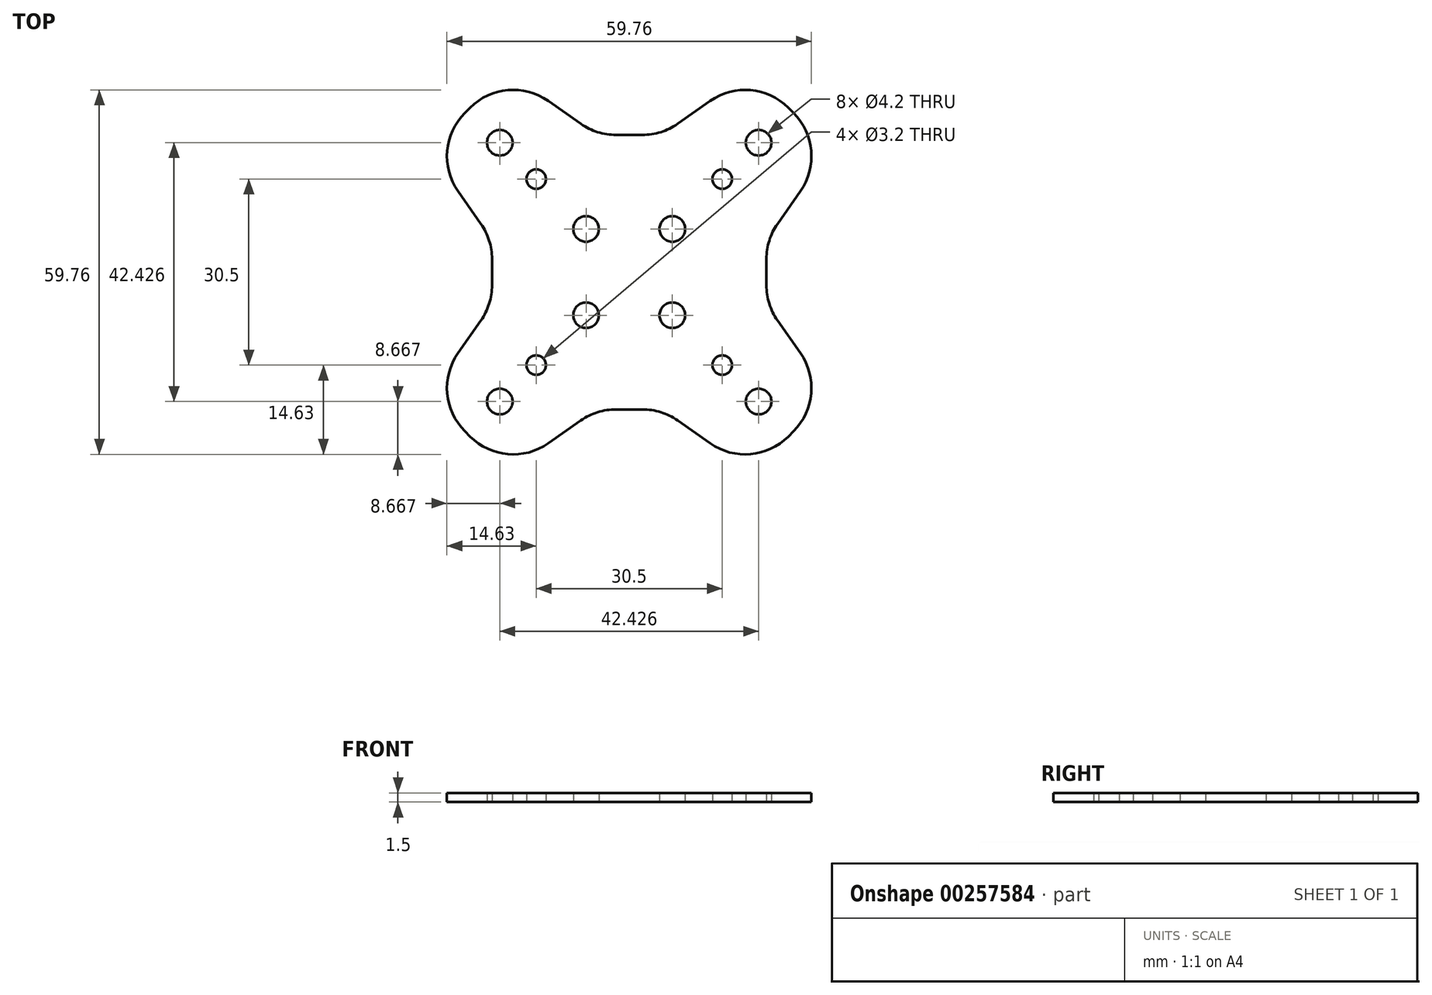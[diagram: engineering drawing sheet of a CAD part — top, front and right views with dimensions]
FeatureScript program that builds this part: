
annotation { "Feature Type Name" : "Feature", "Feature Type Description" : "" }
export const myFeature = defineFeature(function(context is Context, id is Id, definition is map)
    precondition{}
    {
        {
            var Q0;
            Q0=qCreatedBy(makeId("Top.planeOp"),FACE);
            var sketch = newSketch(context, id + "F0", { "sketchPlane" : qUnion([Q0])});
            skLineSegment(sketch, "E0", {"start": v(-32.88, 20.15) * mm, "end": v(-20.15, 32.88) * mm});
            skLineSegment(sketch, "E1", {"start": v(-20.15, 32.88) * mm, "end": v(-5.33, 22.5) * mm});
            skLineSegment(sketch, "E2", {"start": v(-32.88, 20.15) * mm, "end": v(-22.5, 5.33) * mm});
            skLineSegment(sketch, "E3", {"start": v(0, 0) * mm, "end": v(-26.52, 26.52) * mm, "construction": true});
            skLineSegment(sketch, "E4.MirrorCS", {"start": v(32.88, 20.15) * mm, "end": v(20.15, 32.88) * mm});
            skLineSegment(sketch, "E5.MirrorCS", {"start": v(32.88, 20.15) * mm, "end": v(22.5, 5.33) * mm});
            skLineSegment(sketch, "E6.MirrorCS", {"start": v(20.15, 32.88) * mm, "end": v(5.33, 22.5) * mm});
            skLineSegment(sketch, "E7.MirrorCS", {"start": v(20.15, -32.88) * mm, "end": v(5.33, -22.5) * mm});
            skLineSegment(sketch, "E8.MirrorCS", {"start": v(-32.88, -20.15) * mm, "end": v(-20.15, -32.88) * mm});
            skLineSegment(sketch, "E9.MirrorCS", {"start": v(32.88, -20.15) * mm, "end": v(22.5, -5.33) * mm});
            skLineSegment(sketch, "E10.MirrorCS", {"start": v(-32.88, -20.15) * mm, "end": v(-22.5, -5.33) * mm});
            skLineSegment(sketch, "E11.MirrorCS", {"start": v(-20.15, -32.88) * mm, "end": v(-5.33, -22.5) * mm});
            skLineSegment(sketch, "E12.MirrorCS", {"start": v(32.88, -20.15) * mm, "end": v(20.15, -32.88) * mm});
            skLineSegment(sketch, "E13", {"start": v(-5.33, 22.5) * mm, "end": v(5.33, 22.5) * mm});
            skLineSegment(sketch, "E14", {"start": v(22.5, 5.33) * mm, "end": v(22.5, -5.33) * mm});
            skLineSegment(sketch, "E15", {"start": v(5.33, -22.5) * mm, "end": v(-5.33, -22.5) * mm});
            skLineSegment(sketch, "E16", {"start": v(-22.5, -5.33) * mm, "end": v(-22.5, 5.33) * mm});
            skCircle(sketch, "E17", {"center": v(-7.07, 7.07) * mm, "radius": 2.1 * mm});
            skCircle(sketch, "E18", {"center": v(-15.25, 15.25) * mm, "radius": 1.6 * mm});
            skCircle(sketch, "E19", {"center": v(-21.21, 21.21) * mm, "radius": 2.1 * mm});
            skCircle(sketch, "E20.MirrorC", {"center": v(21.21, 21.21) * mm, "radius": 2.1 * mm});
            skCircle(sketch, "E21.MirrorC", {"center": v(15.25, 15.25) * mm, "radius": 1.6 * mm});
            skCircle(sketch, "E22.MirrorC", {"center": v(7.07, 7.07) * mm, "radius": 2.1 * mm});
            skCircle(sketch, "E23.MirrorC", {"center": v(-21.21, -21.21) * mm, "radius": 2.1 * mm});
            skCircle(sketch, "E24.MirrorC", {"center": v(-15.25, -15.25) * mm, "radius": 1.6 * mm});
            skCircle(sketch, "E25.MirrorC", {"center": v(-7.07, -7.07) * mm, "radius": 2.1 * mm});
            skCircle(sketch, "E26.MirrorC", {"center": v(21.21, -21.21) * mm, "radius": 2.1 * mm});
            skCircle(sketch, "E27.MirrorC", {"center": v(15.25, -15.25) * mm, "radius": 1.6 * mm});
            skCircle(sketch, "E28.MirrorC", {"center": v(7.07, -7.07) * mm, "radius": 2.1 * mm});
            skSolve(sketch);
        }
        {
            var Q0;
            Q0 = qSketchRegion(id + "F0", true);
            extrude(context, id + "F1", {"entities" : qUnion([Q0]), "depth" : 1.5 * mm});
        }
        {
            var Q0;
            Q0=makeQuery(id+"F1.opExtrude","SWEPT_EDGE",EDGE,{"disambiguationData":[OSD([sQuery(id+"F0.wireOp",EDGE,"E0"),sQuery(id+"F0.wireOp",EDGE,"E2")])]});
            var Q1;
            Q1=makeQuery(id+"F1.opExtrude","SWEPT_EDGE",EDGE,{"disambiguationData":[OSD([sQuery(id+"F0.wireOp",EDGE,"E2"),sQuery(id+"F0.wireOp",EDGE,"E16")])]});
            var Q2;
            Q2=makeQuery(id+"F1.opExtrude","SWEPT_EDGE",EDGE,{"disambiguationData":[OSD([sQuery(id+"F0.wireOp",EDGE,"E10.MirrorCS"),sQuery(id+"F0.wireOp",EDGE,"E16")])]});
            var Q3;
            Q3=makeQuery(id+"F1.opExtrude","SWEPT_EDGE",EDGE,{"disambiguationData":[OSD([sQuery(id+"F0.wireOp",EDGE,"E8.MirrorCS"),sQuery(id+"F0.wireOp",EDGE,"E10.MirrorCS")])]});
            var Q4;
            Q4=makeQuery(id+"F1.opExtrude","SWEPT_EDGE",EDGE,{"disambiguationData":[OSD([sQuery(id+"F0.wireOp",EDGE,"E8.MirrorCS"),sQuery(id+"F0.wireOp",EDGE,"E11.MirrorCS")])]});
            var Q5;
            Q5=makeQuery(id+"F1.opExtrude","SWEPT_EDGE",EDGE,{"disambiguationData":[OSD([sQuery(id+"F0.wireOp",EDGE,"E11.MirrorCS"),sQuery(id+"F0.wireOp",EDGE,"E15")])]});
            var Q6;
            Q6=makeQuery(id+"F1.opExtrude","SWEPT_EDGE",EDGE,{"disambiguationData":[OSD([sQuery(id+"F0.wireOp",EDGE,"E7.MirrorCS"),sQuery(id+"F0.wireOp",EDGE,"E15")])]});
            var Q7;
            Q7=makeQuery(id+"F1.opExtrude","SWEPT_EDGE",EDGE,{"disambiguationData":[OSD([sQuery(id+"F0.wireOp",EDGE,"E7.MirrorCS"),sQuery(id+"F0.wireOp",EDGE,"E12.MirrorCS")])]});
            var Q8;
            Q8=makeQuery(id+"F1.opExtrude","SWEPT_EDGE",EDGE,{"disambiguationData":[OSD([sQuery(id+"F0.wireOp",EDGE,"E9.MirrorCS"),sQuery(id+"F0.wireOp",EDGE,"E12.MirrorCS")])]});
            var Q9;
            Q9=makeQuery(id+"F1.opExtrude","SWEPT_EDGE",EDGE,{"disambiguationData":[OSD([sQuery(id+"F0.wireOp",EDGE,"E9.MirrorCS"),sQuery(id+"F0.wireOp",EDGE,"E14")])]});
            var Q10;
            Q10=makeQuery(id+"F1.opExtrude","SWEPT_EDGE",EDGE,{"disambiguationData":[OSD([sQuery(id+"F0.wireOp",EDGE,"E5.MirrorCS"),sQuery(id+"F0.wireOp",EDGE,"E14")])]});
            var Q11;
            Q11=makeQuery(id+"F1.opExtrude","SWEPT_EDGE",EDGE,{"disambiguationData":[OSD([sQuery(id+"F0.wireOp",EDGE,"E4.MirrorCS"),sQuery(id+"F0.wireOp",EDGE,"E5.MirrorCS")])]});
            var Q12;
            Q12=makeQuery(id+"F1.opExtrude","SWEPT_EDGE",EDGE,{"disambiguationData":[OSD([sQuery(id+"F0.wireOp",EDGE,"E0"),sQuery(id+"F0.wireOp",EDGE,"E1")])]});
            var Q13;
            Q13=makeQuery(id+"F1.opExtrude","SWEPT_EDGE",EDGE,{"disambiguationData":[OSD([sQuery(id+"F0.wireOp",EDGE,"E4.MirrorCS"),sQuery(id+"F0.wireOp",EDGE,"E6.MirrorCS")])]});
            var Q14;
            Q14=makeQuery(id+"F1.opExtrude","SWEPT_EDGE",EDGE,{"disambiguationData":[OSD([sQuery(id+"F0.wireOp",EDGE,"E6.MirrorCS"),sQuery(id+"F0.wireOp",EDGE,"E13")])]});
            var Q15;
            Q15=makeQuery(id+"F1.opExtrude","SWEPT_EDGE",EDGE,{"disambiguationData":[OSD([sQuery(id+"F0.wireOp",EDGE,"E1"),sQuery(id+"F0.wireOp",EDGE,"E13")])]});
            fillet(context, id + "F2", {"entities" : qUnion([Q0, Q1, Q2, Q3, Q4, Q5, Q6, Q7, Q8, Q9, Q10, Q11, Q12, Q13, Q14, Q15]), "radius" : 10 * mm, "tangentPropagation" : true, "allowEdgeOverflow" : false});
        }
    });
